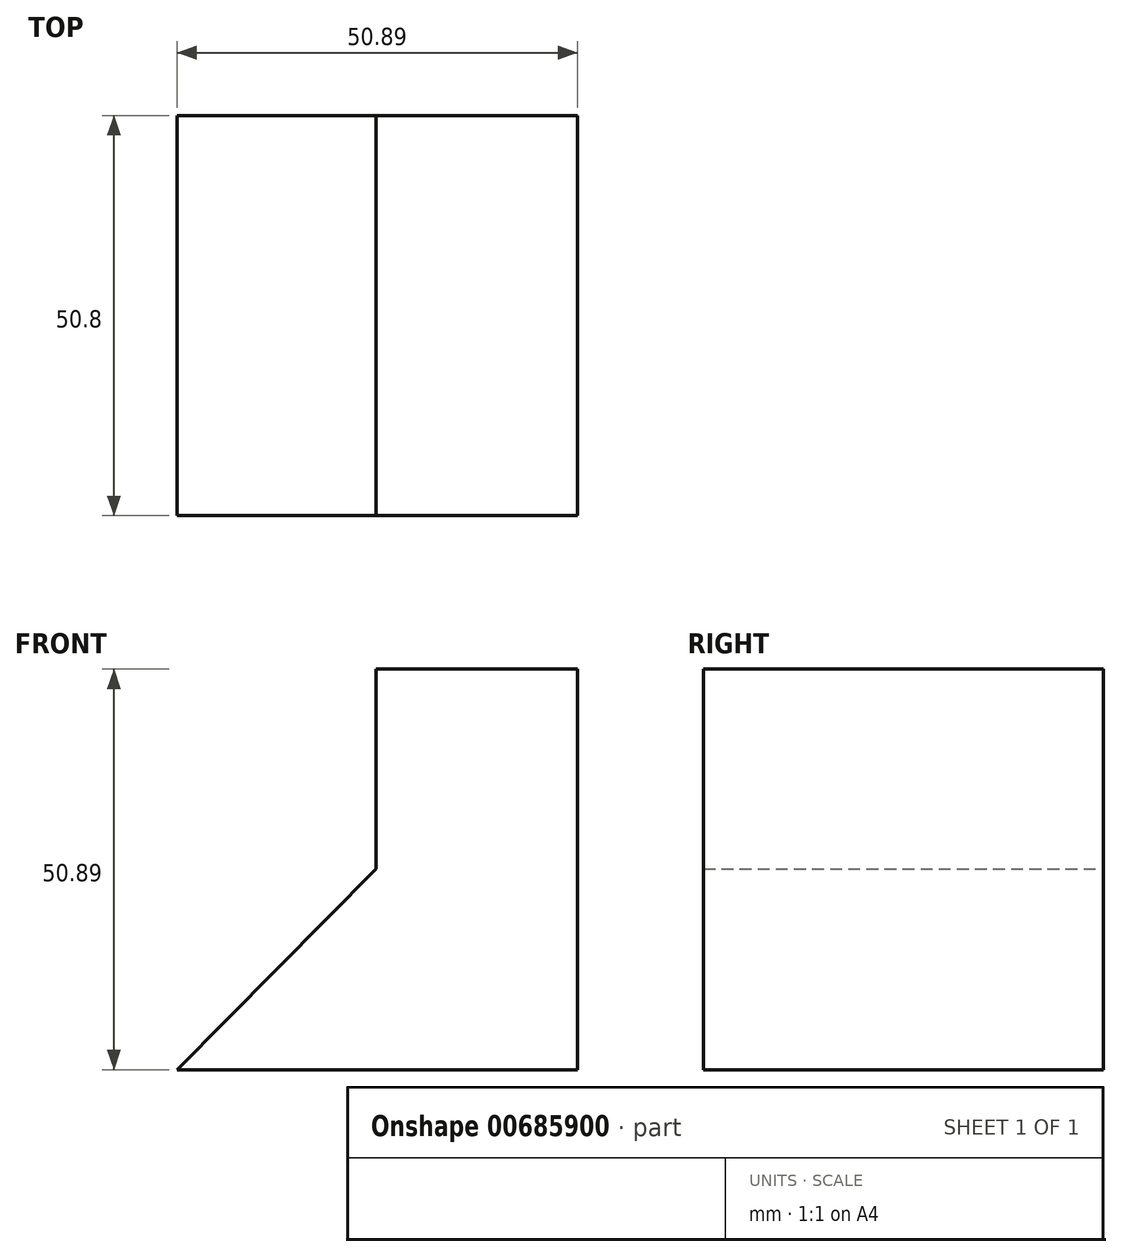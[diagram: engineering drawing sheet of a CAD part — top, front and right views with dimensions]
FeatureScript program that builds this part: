
annotation { "Feature Type Name" : "Feature", "Feature Type Description" : "" }
export const myFeature = defineFeature(function(context is Context, id is Id, definition is map)
    precondition{}
    {
        {
            var Q0;
            Q0=qCreatedBy(makeId("Front.planeOp"),FACE);
            var sketch = newSketch(context, id + "F0", { "sketchPlane" : qUnion([Q0])});
            skLineSegment(sketch, "E0", {"start": v(0, 0) * mm, "end": v(50.89, 0) * mm});
            skLineSegment(sketch, "E1", {"start": v(50.89, 0) * mm, "end": v(50.89, 50.89) * mm});
            skLineSegment(sketch, "E2", {"start": v(50.89, 50.89) * mm, "end": v(25.3, 50.89) * mm});
            skLineSegment(sketch, "E3", {"start": v(25.3, 50.89) * mm, "end": v(25.3, 25.5) * mm});
            skLineSegment(sketch, "E4", {"start": v(25.3, 25.5) * mm, "end": v(0, 0) * mm});
            skSolve(sketch);
        }
        {
            var Q0;
            Q0 = qSketchRegion(id + "F0", true);
            extrude(context, id + "F1", {"entities" : qUnion([Q0]), "depth" : 50.8 * mm, "offsetDistance" : 25.4 * mm});
        }
    });
